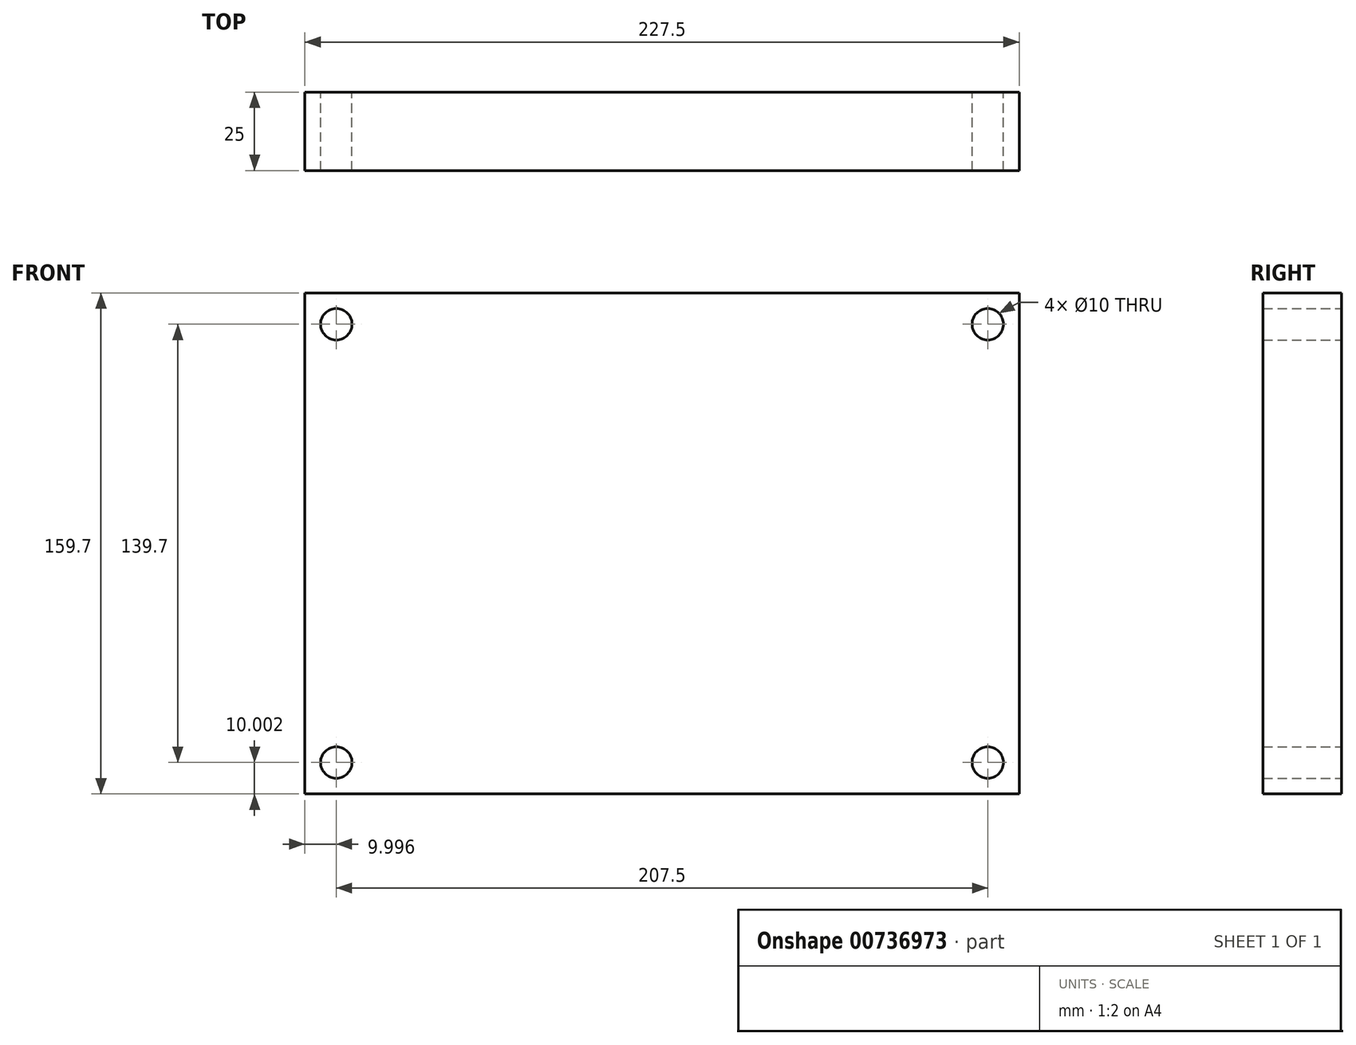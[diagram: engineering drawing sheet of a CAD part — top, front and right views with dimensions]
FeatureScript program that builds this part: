
annotation { "Feature Type Name" : "Feature", "Feature Type Description" : "" }
export const myFeature = defineFeature(function(context is Context, id is Id, definition is map)
    precondition{}
    {
        {
            var Q0;
            Q0=qCreatedBy(makeId("Front.planeOp"),FACE);
            var sketch = newSketch(context, id + "F0", { "sketchPlane" : qUnion([Q0])});
            skLineSegment(sketch, "E0.bottom", {"start": v(-118.42, 14.33) * mm, "end": v(89.08, 14.33) * mm, "construction": true});
            skLineSegment(sketch, "E0.top", {"start": v(-118.42, -125.37) * mm, "end": v(89.08, -125.37) * mm, "construction": true});
            skLineSegment(sketch, "E0.left", {"start": v(-118.42, 14.33) * mm, "end": v(-118.42, -125.37) * mm, "construction": true});
            skLineSegment(sketch, "E0.right", {"start": v(89.08, 14.33) * mm, "end": v(89.08, -125.37) * mm, "construction": true});
            skLineSegment(sketch, "E1.0", {"start": v(99.08, 24.33) * mm, "end": v(99.08, -135.37) * mm});
            skLineSegment(sketch, "E1.1", {"start": v(-128.42, 24.33) * mm, "end": v(99.08, 24.33) * mm});
            skLineSegment(sketch, "E1.2", {"start": v(-128.42, 24.33) * mm, "end": v(-128.42, -135.37) * mm});
            skLineSegment(sketch, "E1.3", {"start": v(-128.42, -135.37) * mm, "end": v(99.08, -135.37) * mm});
            skCircle(sketch, "E2", {"center": v(-118.42, 14.33) * mm, "radius": 5 * mm});
            skCircle(sketch, "E3", {"center": v(89.08, 14.33) * mm, "radius": 5 * mm});
            skCircle(sketch, "E4", {"center": v(89.08, -125.37) * mm, "radius": 5 * mm});
            skCircle(sketch, "E5", {"center": v(-118.42, -125.37) * mm, "radius": 5 * mm});
            skSolve(sketch);
        }
        {
            var Q0;
            Q0 = qSketchRegion(id + "F0", true);
            extrude(context, id + "F1", {"entities" : qUnion([Q0]), "depth" : 25 * mm, "offsetDistance" : 25 * mm});
        }
    });
